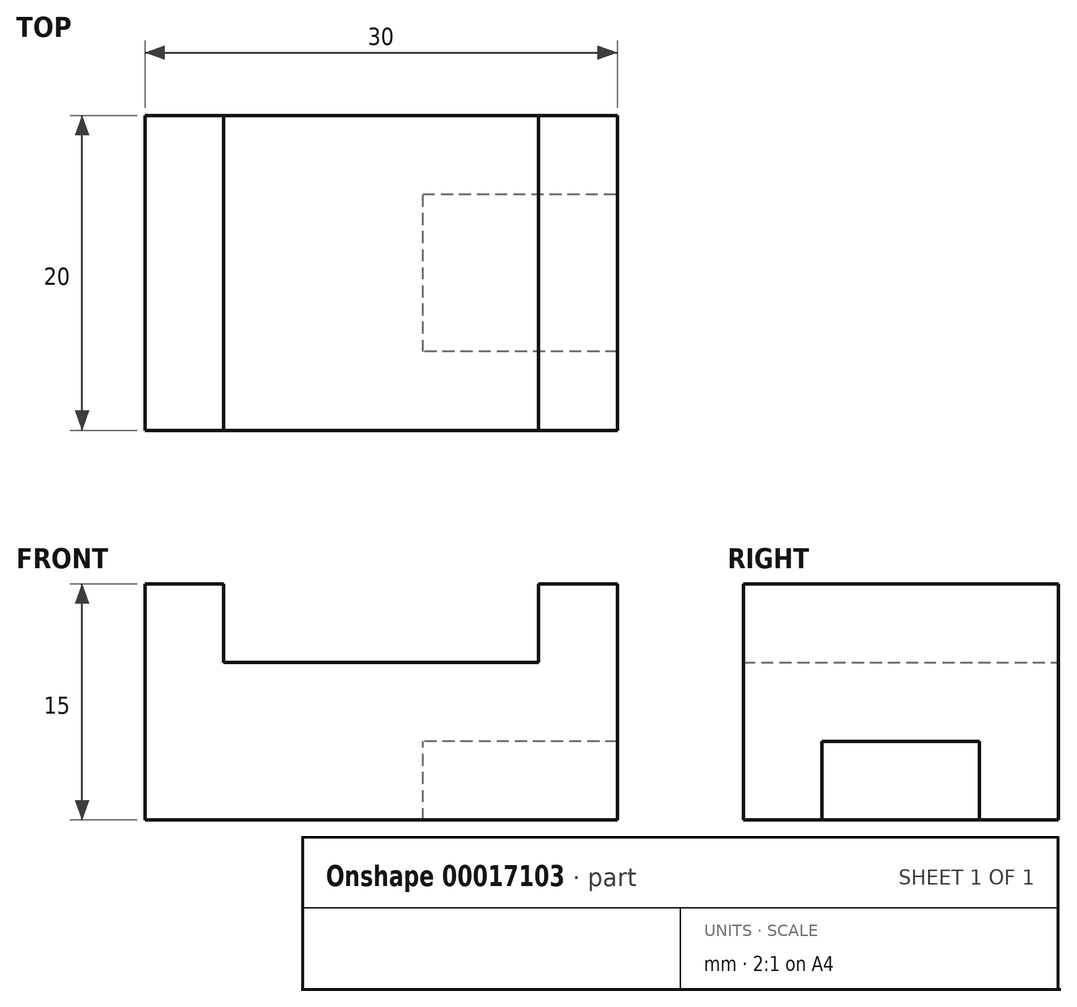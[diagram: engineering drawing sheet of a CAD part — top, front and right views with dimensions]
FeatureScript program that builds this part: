
annotation { "Feature Type Name" : "Feature", "Feature Type Description" : "" }
export const myFeature = defineFeature(function(context is Context, id is Id, definition is map)
    precondition{}
    {
        {
            var Q0;
            Q0=qCreatedBy(makeId("Front.planeOp"),FACE);
            var sketch = newSketch(context, id + "F0", { "sketchPlane" : qUnion([Q0])});
            skLineSegment(sketch, "E0", {"start": v(-17.65, 5.37) * mm, "end": v(-12.65, 5.37) * mm});
            skLineSegment(sketch, "E1", {"start": v(-17.65, 5.37) * mm, "end": v(-17.65, 0) * mm});
            skLineSegment(sketch, "E2", {"start": v(-12.65, 5.37) * mm, "end": v(-12.65, 0.37) * mm});
            skLineSegment(sketch, "E3", {"start": v(-12.65, 0.37) * mm, "end": v(7.35, 0.37) * mm});
            skLineSegment(sketch, "E4", {"start": v(7.35, 0.37) * mm, "end": v(7.35, 5.37) * mm});
            skLineSegment(sketch, "E5", {"start": v(7.35, 5.37) * mm, "end": v(12.35, 5.37) * mm});
            skLineSegment(sketch, "E6", {"start": v(12.35, 5.37) * mm, "end": v(12.35, -9.63) * mm});
            skLineSegment(sketch, "E7", {"start": v(-17.65, 0) * mm, "end": v(-17.65, -9.63) * mm});
            skLineSegment(sketch, "E8", {"start": v(-17.65, -9.63) * mm, "end": v(12.35, -9.63) * mm});
            skSolve(sketch);
        }
        {
            var Q0;
            Q0=makeQuery(id+"F0.imprint","IMPRINT",FACE,{"disambiguationData":[TD([[makeQuery(id+"F0.imprint","IMPRINT",EDGE,{"derivedFrom":sQuery(id+"F0.wireOp",EDGE,"E0")}),-1.0]])]});
            extrude(context, id + "F1", {"entities" : qUnion([Q0]), "depth" : 20 * mm});
        }
        {
            var Q0;
            Q0=qCreatedBy(makeId("Right.planeOp"),FACE);
            var sketch = newSketch(context, id + "F2", { "sketchPlane" : qUnion([Q0])});
            skPoint(sketch, "E9", {"position": v(-15, -9.83) * mm});
            skPoint(sketch, "E10", {"position": v(-5, -9.83) * mm});
            skPoint(sketch, "E11", {"position": v(-5, -4.63) * mm});
            skPoint(sketch, "E12", {"position": v(-15, -4.63) * mm});
            skLineSegment(sketch, "E13", {"start": v(-15, -4.63) * mm, "end": v(-15, -9.83) * mm});
            skLineSegment(sketch, "E14", {"start": v(-15, -9.83) * mm, "end": v(-5, -9.83) * mm});
            skLineSegment(sketch, "E15", {"start": v(-5, -9.83) * mm, "end": v(-5, -4.63) * mm});
            skLineSegment(sketch, "E16", {"start": v(-5, -4.63) * mm, "end": v(-15, -4.63) * mm});
            skSolve(sketch);
        }
        {
            var Q0;
            Q0=makeQuery(id+"F2.imprint","IMPRINT",FACE,{"disambiguationData":[TD([[makeQuery(id+"F2.imprint","IMPRINT",EDGE,{"derivedFrom":sQuery(id+"F2.wireOp",EDGE,"E13")}),1.0]])]});
            extrude(context, id + "F3", {"entities" : qUnion([Q0]), "operationType" : NewBodyOperationType.REMOVE, "endBound" : BoundingType.THROUGH_ALL, "depth" : 25 * mm});
        }
    });
